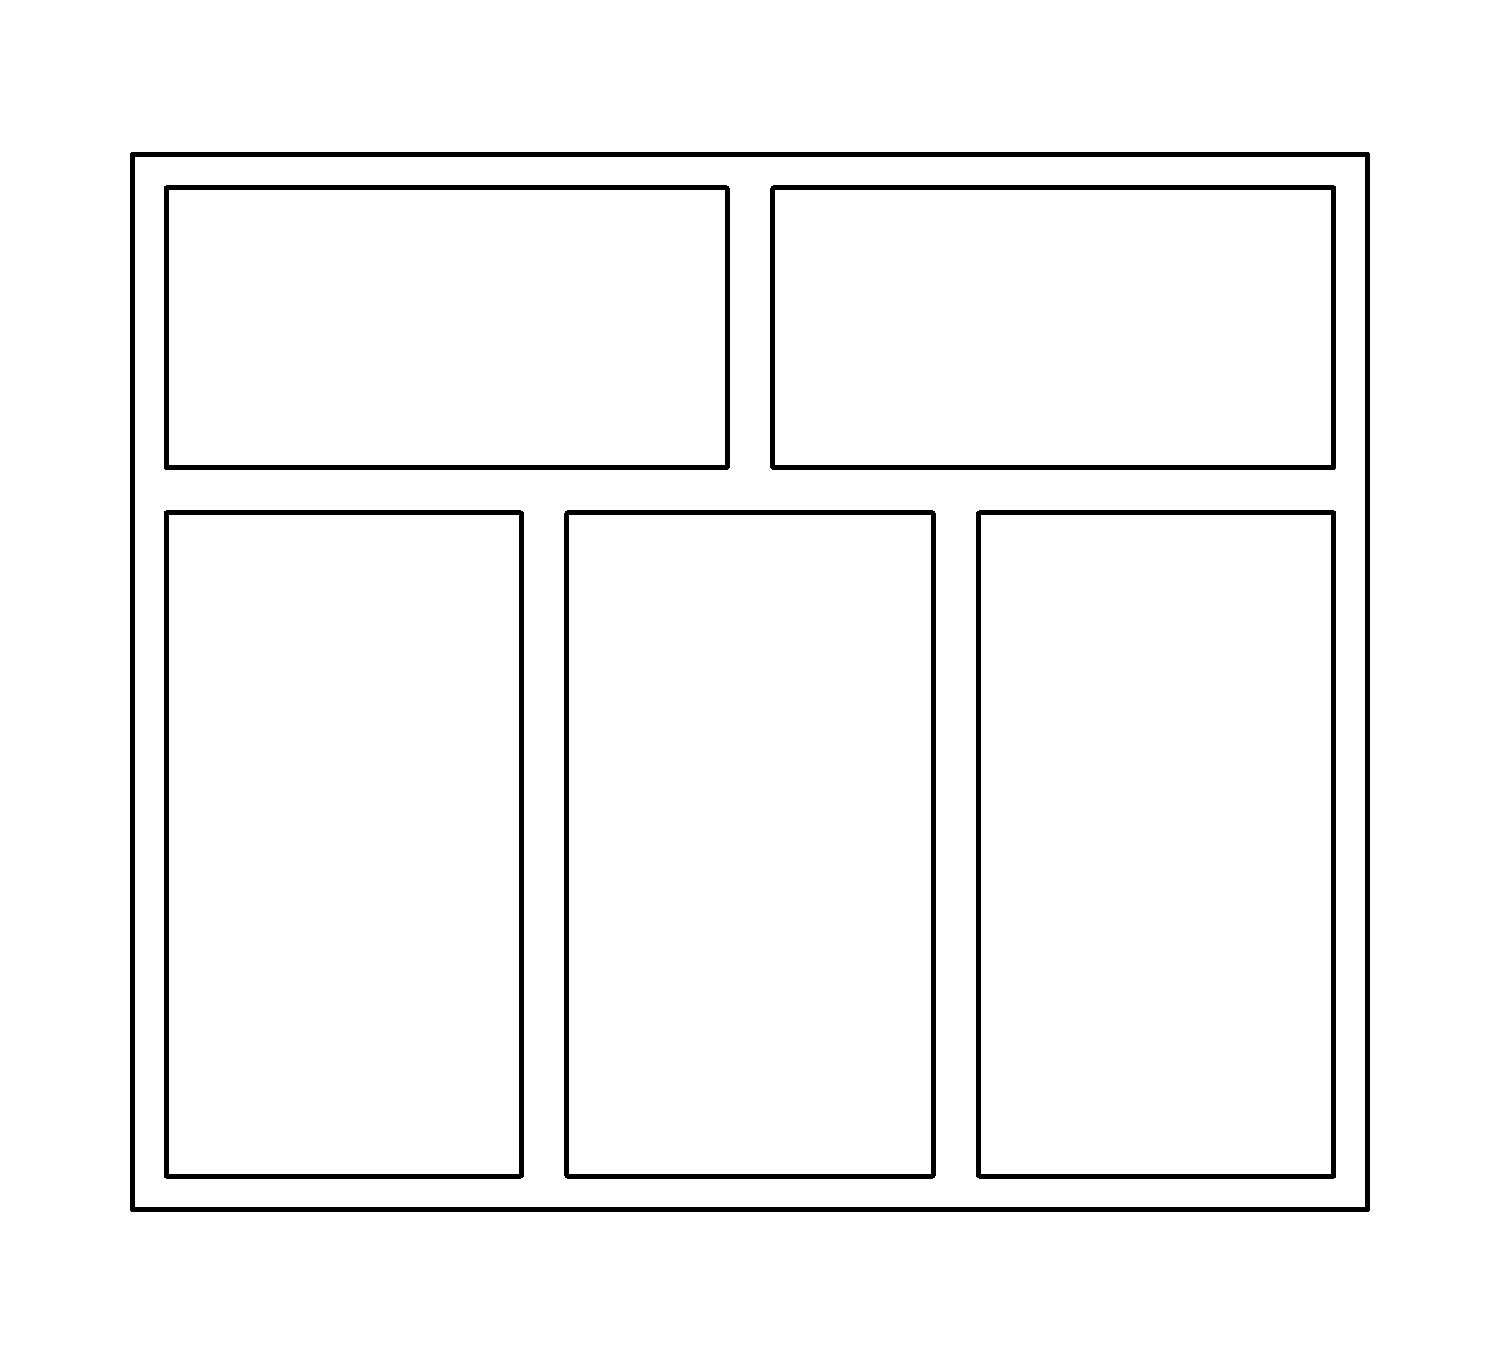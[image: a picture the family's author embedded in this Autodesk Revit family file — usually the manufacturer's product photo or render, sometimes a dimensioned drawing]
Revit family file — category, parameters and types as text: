
# Revit family: окна.rehau_трехпольное_2_фрамуги_сверху
name_source: partatom
category: Окна
revit_build: Autodesk Revit 2017 (Build: 20171027_0315(x64)
units: mm (PartAtom-declared; Revit-internal decimal feet)

## family parameters
Всегда вертикально = Да
Заголовок OmniClass = Windows
Номер OmniClass = 23.30.20.00
Общий = Нет
Основа = Стена
При загрузке вырезать с полостями = Нет
Точка расчета площади = Нет

## types (2) — shared parameters
24_мм = 24мм 1-камерный
32_мм = 32мм 2-камерный
40_мм = 40мм 2-камерный
42_мм = 42мм 2-камерный
50_мм = 50мм 2-камерный
60_blitz_new = 60 BLITZ NEW
60_euro_64 = 60 EURO (коробка 64, импост 78, створка 60)
60_euro_68 = 60 EURO (коробка 68, импост 78, створка 60)
60_euro_76 = 60 EURO (коробка 76, импост 86, створка 74)
70_delight_78 = 70 DELIGHT
70_grazio_55 = 70 GRAZIO (коробка 55)
70_grazio_63 = 70 GRAZIO (коробка 63)
80_intelio_58r = 80 INTELIO (коробка 58, створка R57)
80_intelio_58z = 80 INTELIO (коробка 58, створка Z57)
80_intelio_65r = 80 INTELIO (коробка 65, створка R57)
80_intelio_65z = 80 INTELIO (коробка 65, створка Z57)
ADSK_Обозначение = ГОСТ 30674-99
URL = https://www.rehau.com
sp_energy = Энергосберегающие стекла
sp_gaz = Заполненный газом
sp_standart = Обычный стеклопакет
sp_triplex = Триплекс
Аналитическая конструкция = Окна с одинарным остеклением - для жилых зданий
Высота подоконника по умолчанию = 900 мм
Высота створок = 1200 мм
Группа модели = ОП
Замыкание стены = По основе
Изготовитель = Rehau
Изображение типоразмера = схема_трехпольное_2_фрамуги_сверху.png
Коэффициент теплопередачи (U) = 5.7361 Вт/(м²·K)
Коэффициент теплопритока от солнечного излучения = 0.86
Материал коробки = <По категории>
Материал отлива = <По категории>
Материал подоконника = <По категории>
Материал стекла = <По категории>
Описание = проем.окно
Примерная высота = 1760 мм
Примерная ширина = 2060 мм
Пропускание видимого света = 0.9
Равные створки = Да
Створка слева = 400 мм
Створка справа = 400 мм
Термостойкость = 0.1743 (м²·K)/Вт
Тип створки центр = створка : глухая
Тип фрамуги слева = створка : глухая
Тип фрамуги справа = створка : глухая
глухая_створка = створка : глухая
обозначение_проема_высота = 293 мм
обозначение_проема_ширина = 343 мм
таблица выбора = каталог профилей Rehau

## per-type parameters (varying)
| type | Тип створки слева | Тип створки справа |
| 2060х1760 (2 створки и глухое) | створка : левая-откидная | створка : правая-откидная |
| 2060х1760 (глухое) | створка : глухая | створка : глухая |
